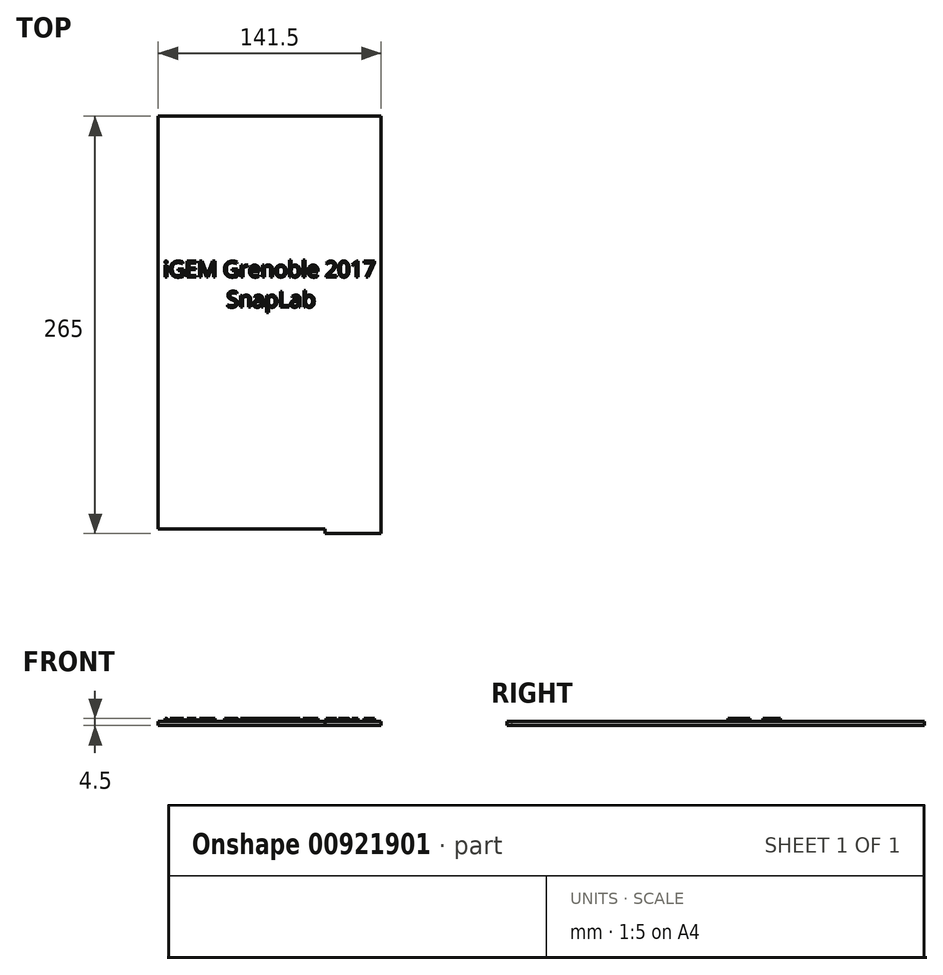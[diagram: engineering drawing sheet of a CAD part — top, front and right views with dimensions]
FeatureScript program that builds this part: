
annotation { "Feature Type Name" : "Feature", "Feature Type Description" : "" }
export const myFeature = defineFeature(function(context is Context, id is Id, definition is map)
    precondition{}
    {
        {
            var Q0;
            Q0=qCreatedBy(makeId("Top.planeOp"),FACE);
            var sketch = newSketch(context, id + "F0", { "sketchPlane" : qUnion([Q0])});
            skLineSegment(sketch, "E0", {"start": v(0, 0) * mm, "end": v(0, 262) * mm});
            skLineSegment(sketch, "E1", {"start": v(0, 262) * mm, "end": v(141.5, 262) * mm});
            skLineSegment(sketch, "E2", {"start": v(141.5, 262) * mm, "end": v(141.5, -3) * mm});
            skLineSegment(sketch, "E3", {"start": v(141.5, -3) * mm, "end": v(106, -3) * mm});
            skLineSegment(sketch, "E4", {"start": v(106, -3) * mm, "end": v(106, 0) * mm});
            skLineSegment(sketch, "E5", {"start": v(106, 0) * mm, "end": v(0, 0) * mm});
            skSolve(sketch);
        }
        {
            var Q0;
            Q0=makeQuery(id+"F0.imprint","IMPRINT",FACE,{"disambiguationData":[TD([[makeQuery(id+"F0.imprint","IMPRINT",EDGE,{"derivedFrom":sQuery(id+"F0.wireOp",EDGE,"E0")}),-1.0]])]});
            extrude(context, id + "F1", {"entities" : qUnion([Q0]), "depth" : 2.5 * mm, "offsetDistance" : 25 * mm});
        }
        {
            var Q0;
            Q0=makeQuery(id+"F1.opExtrude","CAP_FACE",FACE,{"disambiguationData":[OSD([sQuery(id+"F0.wireOp",EDGE,"E0"),sQuery(id+"F0.wireOp",EDGE,"E1"),sQuery(id+"F0.wireOp",EDGE,"E2"),sQuery(id+"F0.wireOp",EDGE,"E3"),sQuery(id+"F0.wireOp",EDGE,"E4"),sQuery(id+"F0.wireOp",EDGE,"E5")])],"isStart":false});
            var sketch = newSketch(context, id + "F2", { "sketchPlane" : qUnion([Q0])});
            skText(sketch, "E6", { "text": "iGEM Grenoble 2017\n           SnapLab", "fontName": "OpenSans-Regular.ttf"});
            const initialGuessF2  = {"E6": [0.00325, 0.15988, 1, 0, 0.01012]};
            skSetInitialGuess(sketch, initialGuessF2);
            skSolve(sketch);
        }
        {
            var Q0;
            Q0=makeQuery(id+"F2.imprint","IMPRINT",FACE,{"disambiguationData":[TD([[makeQuery(id+"F2.imprint","IMPRINT",EDGE,{"derivedFrom":sQuery(id+"F2.wireOp",EDGE,"E6.sketch_text.stroke-0")}),-1.0]])]});
            var Q1;
            Q1=makeQuery(id+"F2.imprint","IMPRINT",FACE,{"disambiguationData":[TD([[makeQuery(id+"F2.imprint","IMPRINT",EDGE,{"derivedFrom":sQuery(id+"F2.wireOp",EDGE,"E6.sketch_text.stroke-4")}),-1.0]])]});
            var Q2;
            Q2=makeQuery(id+"F2.imprint","IMPRINT",FACE,{"disambiguationData":[TD([[makeQuery(id+"F2.imprint","IMPRINT",EDGE,{"derivedFrom":sQuery(id+"F2.wireOp",EDGE,"E6.sketch_text.stroke-12")}),-1.0]])]});
            var Q3;
            Q3=makeQuery(id+"F2.imprint","IMPRINT",FACE,{"disambiguationData":[TD([[makeQuery(id+"F2.imprint","IMPRINT",EDGE,{"derivedFrom":sQuery(id+"F2.wireOp",EDGE,"E6.sketch_text.stroke-32")}),-1.0]])]});
            var Q4;
            Q4=makeQuery(id+"F2.imprint","IMPRINT",FACE,{"disambiguationData":[TD([[makeQuery(id+"F2.imprint","IMPRINT",EDGE,{"derivedFrom":sQuery(id+"F2.wireOp",EDGE,"E6.sketch_text.stroke-44")}),-1.0]])]});
            var Q5;
            Q5=makeQuery(id+"F2.imprint","IMPRINT",FACE,{"disambiguationData":[TD([[makeQuery(id+"F2.imprint","IMPRINT",EDGE,{"derivedFrom":sQuery(id+"F2.wireOp",EDGE,"E6.sketch_text.stroke-62")}),-1.0]])]});
            var Q6;
            Q6=makeQuery(id+"F2.imprint","IMPRINT",FACE,{"disambiguationData":[TD([[makeQuery(id+"F2.imprint","IMPRINT",EDGE,{"derivedFrom":sQuery(id+"F2.wireOp",EDGE,"E6.sketch_text.stroke-82")}),-1.0]])]});
            var Q7;
            Q7=makeQuery(id+"F2.imprint","IMPRINT",FACE,{"disambiguationData":[TD([[makeQuery(id+"F2.imprint","IMPRINT",EDGE,{"derivedFrom":sQuery(id+"F2.wireOp",EDGE,"E6.sketch_text.stroke-95")}),-1.0]])]});
            var Q8;
            Q8=makeQuery(id+"F2.imprint","IMPRINT",FACE,{"disambiguationData":[TD([[makeQuery(id+"F2.imprint","IMPRINT",EDGE,{"derivedFrom":sQuery(id+"F2.wireOp",EDGE,"E6.sketch_text.stroke-114")}),-1.0]])]});
            var Q9;
            Q9=makeQuery(id+"F2.imprint","IMPRINT",FACE,{"disambiguationData":[TD([[makeQuery(id+"F2.imprint","IMPRINT",EDGE,{"derivedFrom":sQuery(id+"F2.wireOp",EDGE,"E6.sketch_text.stroke-131")}),-1.0]])]});
            var Q10;
            Q10=makeQuery(id+"F2.imprint","IMPRINT",FACE,{"disambiguationData":[TD([[makeQuery(id+"F2.imprint","IMPRINT",EDGE,{"derivedFrom":sQuery(id+"F2.wireOp",EDGE,"E6.sketch_text.stroke-148")}),-1.0]])]});
            var Q11;
            Q11=makeQuery(id+"F2.imprint","IMPRINT",FACE,{"disambiguationData":[TD([[makeQuery(id+"F2.imprint","IMPRINT",EDGE,{"derivedFrom":sQuery(id+"F2.wireOp",EDGE,"E6.sketch_text.stroke-171")}),-1.0]])]});
            var Q12;
            Q12=makeQuery(id+"F2.imprint","IMPRINT",FACE,{"disambiguationData":[TD([[makeQuery(id+"F2.imprint","IMPRINT",EDGE,{"derivedFrom":sQuery(id+"F2.wireOp",EDGE,"E6.sketch_text.stroke-175")}),-1.0]])]});
            var Q13;
            Q13=makeQuery(id+"F2.imprint","IMPRINT",FACE,{"disambiguationData":[TD([[makeQuery(id+"F2.imprint","IMPRINT",EDGE,{"derivedFrom":sQuery(id+"F2.wireOp",EDGE,"E6.sketch_text.stroke-194")}),-1.0]])]});
            var Q14;
            Q14=makeQuery(id+"F2.imprint","IMPRINT",FACE,{"disambiguationData":[TD([[makeQuery(id+"F2.imprint","IMPRINT",EDGE,{"derivedFrom":sQuery(id+"F2.wireOp",EDGE,"E6.sketch_text.stroke-214")}),-1.0]])]});
            var Q15;
            Q15=makeQuery(id+"F2.imprint","IMPRINT",FACE,{"disambiguationData":[TD([[makeQuery(id+"F2.imprint","IMPRINT",EDGE,{"derivedFrom":sQuery(id+"F2.wireOp",EDGE,"E6.sketch_text.stroke-230")}),-1.0]])]});
            var Q16;
            Q16=makeQuery(id+"F2.imprint","IMPRINT",FACE,{"disambiguationData":[TD([[makeQuery(id+"F2.imprint","IMPRINT",EDGE,{"derivedFrom":sQuery(id+"F2.wireOp",EDGE,"E6.sketch_text.stroke-239")}),-1.0]])]});
            var Q17;
            Q17=makeQuery(id+"F2.imprint","IMPRINT",FACE,{"disambiguationData":[TD([[makeQuery(id+"F2.imprint","IMPRINT",EDGE,{"derivedFrom":sQuery(id+"F2.wireOp",EDGE,"E6.sketch_text.stroke-246")}),-1.0]])]});
            var Q18;
            Q18=makeQuery(id+"F2.imprint","IMPRINT",FACE,{"disambiguationData":[TD([[makeQuery(id+"F2.imprint","IMPRINT",EDGE,{"derivedFrom":sQuery(id+"F2.wireOp",EDGE,"E6.sketch_text.stroke-271")}),-1.0]])]});
            var Q19;
            Q19=makeQuery(id+"F2.imprint","IMPRINT",FACE,{"disambiguationData":[TD([[makeQuery(id+"F2.imprint","IMPRINT",EDGE,{"derivedFrom":sQuery(id+"F2.wireOp",EDGE,"E6.sketch_text.stroke-288")}),-1.0]])]});
            var Q20;
            Q20=makeQuery(id+"F2.imprint","IMPRINT",FACE,{"disambiguationData":[TD([[makeQuery(id+"F2.imprint","IMPRINT",EDGE,{"derivedFrom":sQuery(id+"F2.wireOp",EDGE,"E6.sketch_text.stroke-315")}),-1.0]])]});
            var Q21;
            Q21=makeQuery(id+"F2.imprint","IMPRINT",FACE,{"disambiguationData":[TD([[makeQuery(id+"F2.imprint","IMPRINT",EDGE,{"derivedFrom":sQuery(id+"F2.wireOp",EDGE,"E6.sketch_text.stroke-340")}),-1.0]])]});
            var Q22;
            Q22=makeQuery(id+"F2.imprint","IMPRINT",FACE,{"disambiguationData":[TD([[makeQuery(id+"F2.imprint","IMPRINT",EDGE,{"derivedFrom":sQuery(id+"F2.wireOp",EDGE,"E6.sketch_text.stroke-346")}),-1.0]])]});
            var Q23;
            Q23=makeQuery(id+"F2.imprint","IMPRINT",FACE,{"disambiguationData":[TD([[makeQuery(id+"F2.imprint","IMPRINT",EDGE,{"derivedFrom":sQuery(id+"F2.wireOp",EDGE,"E6.sketch_text.stroke-373")}),-1.0]])]});
            extrude(context, id + "F3", {"entities" : qUnion([Q0, Q1, Q2, Q3, Q4, Q5, Q6, Q7, Q8, Q9, Q10, Q11, Q12, Q13, Q14, Q15, Q16, Q17, Q18, Q19, Q20, Q21, Q22, Q23]), "operationType" : NewBodyOperationType.ADD, "depth" : 2 * mm, "offsetDistance" : 25 * mm});
        }
    });
